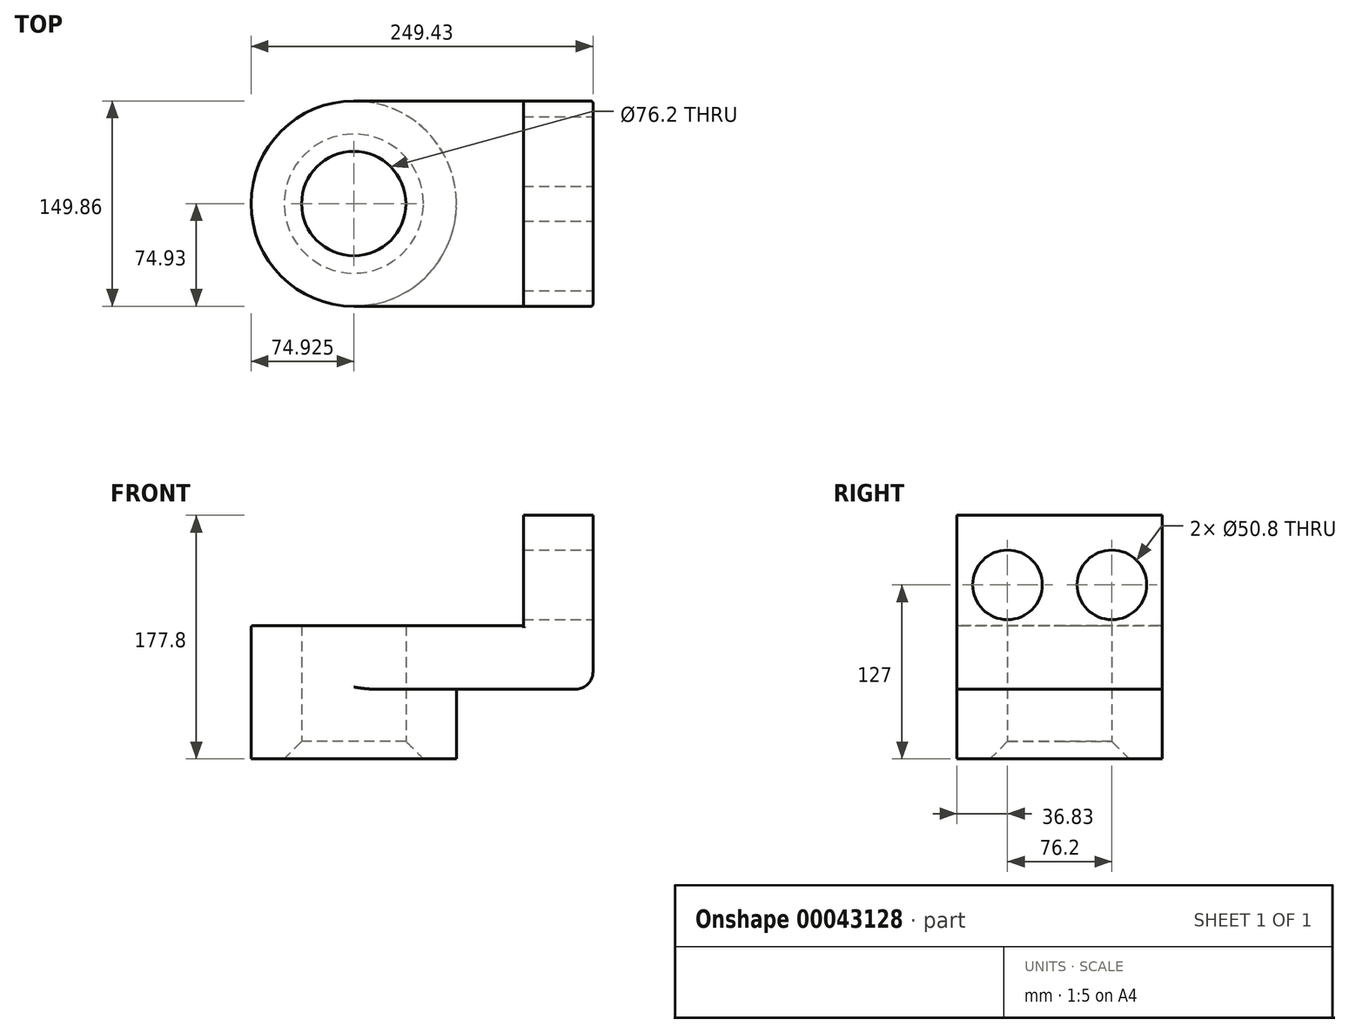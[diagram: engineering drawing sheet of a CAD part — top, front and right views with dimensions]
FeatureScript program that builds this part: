
annotation { "Feature Type Name" : "Feature", "Feature Type Description" : "" }
export const myFeature = defineFeature(function(context is Context, id is Id, definition is map)
    precondition{}
    {
        {
            var Q0;
            Q0=qCreatedBy(makeId("Top.planeOp"),FACE);
            var sketch = newSketch(context, id + "F0", { "sketchPlane" : qUnion([Q0])});
            skLineSegment(sketch, "E0.rect.bottom", {"start": v(87.25, 74.93) * mm, "end": v(-87.25, 74.93) * mm});
            skLineSegment(sketch, "E0.rect.top", {"start": v(87.25, -74.93) * mm, "end": v(-87.25, -74.93) * mm});
            skLineSegment(sketch, "E0.rect.left", {"start": v(87.25, 74.93) * mm, "end": v(87.25, -74.93) * mm});
            skLineSegment(sketch, "E0.rect.right", {"start": v(-87.25, 74.93) * mm, "end": v(-87.25, -74.93) * mm});
            skPoint(sketch, "E0.rect.middle", {"position": v(0, 0) * mm});
            skCircle(sketch, "E1", {"center": v(-87.25, 0) * mm, "radius": 74.93 * mm});
            skCircle(sketch, "E2", {"center": v(-87.25, 0) * mm, "radius": 38.1 * mm});
            skSolve(sketch);
        }
        {
            var Q0;
            Q0 = qSketchRegion(id + "F0", true);
            extrude(context, id + "F1", {"entities" : qUnion([Q0]), "depth" : 46.56 * mm});
        }
        {
            var Q0;
            {var subQ0=sQuery(id+"F0.wireOp",EDGE,"E2");var subQ1=sQuery(id+"F0.wireOp",EDGE,"E0.rect.right");var subQ3=makeQuery(id+"F0.imprint","INTERSECT",VERTEX,{"disambiguationData":[OD(0.0)],"derivedFrom":[subQ1,subQ0]});Q0=makeQuery(id+"F0.imprint","IMPRINT",FACE,{"disambiguationData":[TD([[makeQuery(id+"F0.imprint","IMPRINT",EDGE,{"disambiguationData":[TD([[subQ3,-1.0]])],"derivedFrom":subQ0}),-1.0]])]});}
            var Q1;
            {var subQ0=sQuery(id+"F0.wireOp",EDGE,"E2");var subQ1=sQuery(id+"F0.wireOp",EDGE,"E0.rect.right");var subQ3=makeQuery(id+"F0.imprint","INTERSECT",VERTEX,{"disambiguationData":[OD(0.0)],"derivedFrom":[subQ1,subQ0]});Q1=makeQuery(id+"F0.imprint","IMPRINT",FACE,{"disambiguationData":[TD([[makeQuery(id+"F0.imprint","IMPRINT",EDGE,{"disambiguationData":[TD([[subQ3,1.0]])],"derivedFrom":subQ0}),-1.0]])]});}
            extrude(context, id + "F2", {"entities" : qUnion([Q0, Q1]), "operationType" : NewBodyOperationType.ADD, "oppositeDirection" : true, "depth" : 50.8 * mm});
        }
        {
            var Q0;
            Q0=makeQuery(id+"F1.opExtrude","SWEPT_FACE",FACE,{"disambiguationData":[OSD([sQuery(id+"F0.wireOp",EDGE,"E0.rect.left")])]});
            var sketch = newSketch(context, id + "F3", { "sketchPlane" : qUnion([Q0])});
            skLineSegment(sketch, "E3.bottom", {"start": v(74.93, 0) * mm, "end": v(-74.93, 0) * mm});
            skLineSegment(sketch, "E3.top", {"start": v(74.93, 127) * mm, "end": v(-74.93, 127) * mm});
            skLineSegment(sketch, "E3.left", {"start": v(74.93, 0) * mm, "end": v(74.93, 127) * mm});
            skLineSegment(sketch, "E3.right", {"start": v(-74.93, 0) * mm, "end": v(-74.93, 127) * mm});
            skCircle(sketch, "E4", {"center": v(38.1, 76.2) * mm, "radius": 25.4 * mm});
            skLineSegment(sketch, "E5", {"start": v(0, 0) * mm, "end": v(0, 127) * mm});
            skCircle(sketch, "E6.MirrorC", {"center": v(-38.1, 76.2) * mm, "radius": 25.4 * mm});
            skSolve(sketch);
        }
        {
            var Q0;
            Q0 = qSketchRegion(id + "F3", true);
            extrude(context, id + "F4", {"entities" : qUnion([Q0]), "operationType" : NewBodyOperationType.ADD, "oppositeDirection" : true, "depth" : 50.8 * mm});
        }
        {
            var Q0;
            Q0=makeQuery(id+"F1.opExtrude","CAP_EDGE",EDGE,{"disambiguationData":[OSD([sQuery(id+"F0.wireOp",EDGE,"E0.rect.left")])],"isStart":true});
            fillet(context, id + "F5", {"entities" : qUnion([Q0]), "radius" : 12.7 * mm, "tangentPropagation" : true, "allowEdgeOverflow" : false});
        }
        {
            var Q0;
            Q0=makeQuery(id+"F1.opExtrude","CAP_EDGE",EDGE,{"disambiguationData":[OSD([sQuery(id+"F0.wireOp",EDGE,"E0.rect.bottom")])],"isStart":true});
            var Q1;
            Q1=makeQuery(id+"F1.opExtrude","CAP_EDGE",EDGE,{"disambiguationData":[OSD([sQuery(id+"F0.wireOp",EDGE,"E0.rect.bottom")])],"isStart":false});
            var Q2;
            Q2=makeQuery(id+"F4.opExtrude","CAP_EDGE",EDGE,{"disambiguationData":[OSD([sQuery(id+"F3.wireOp",EDGE,"E3.left")])],"isStart":false});
            var Q3;
            Q3=makeQuery(id+"F4.boolean.opBoolean","MERGE",EDGE,{"derivedFrom":[makeQuery(id+"F1.opExtrude","SWEPT_EDGE",EDGE,{"disambiguationData":[OSD([sQuery(id+"F0.wireOp",EDGE,"E0.rect.bottom"),sQuery(id+"F0.wireOp",EDGE,"E0.rect.left")])]}),makeQuery(id+"F4.opExtrude","CAP_EDGE",EDGE,{"disambiguationData":[OSD([sQuery(id+"F3.wireOp",EDGE,"E3.left")])],"isStart":true})]});
            var Q4;
            Q4=makeQuery(id+"F4.boolean.opBoolean","MERGE",EDGE,{"derivedFrom":[makeQuery(id+"F1.opExtrude","SWEPT_EDGE",EDGE,{"disambiguationData":[OSD([sQuery(id+"F0.wireOp",EDGE,"E0.rect.top"),sQuery(id+"F0.wireOp",EDGE,"E0.rect.left")])]}),makeQuery(id+"F4.opExtrude","CAP_EDGE",EDGE,{"disambiguationData":[OSD([sQuery(id+"F3.wireOp",EDGE,"E3.right")])],"isStart":true})]});
            var Q5;
            Q5=makeQuery(id+"F1.opExtrude","CAP_EDGE",EDGE,{"disambiguationData":[OSD([sQuery(id+"F0.wireOp",EDGE,"E0.rect.top")])],"isStart":true});
            fillet(context, id + "F6", {"entities" : qUnion([Q0, Q1, Q2, Q3, Q4, Q5]), "radius" : 1.59 * mm, "tangentPropagation" : true, "allowEdgeOverflow" : false});
        }
        {
            var Q0;
            Q0=makeQuery(id+"F2.opExtrude","CAP_EDGE",EDGE,{"disambiguationData":[OSD([sQuery(id+"F0.wireOp",EDGE,"E2")])],"isStart":false});
            chamfer(context, id + "F7", {"entities" : qUnion([Q0]), "width" : 12.7 * mm, "tangentPropagation" : true});
        }
    });
